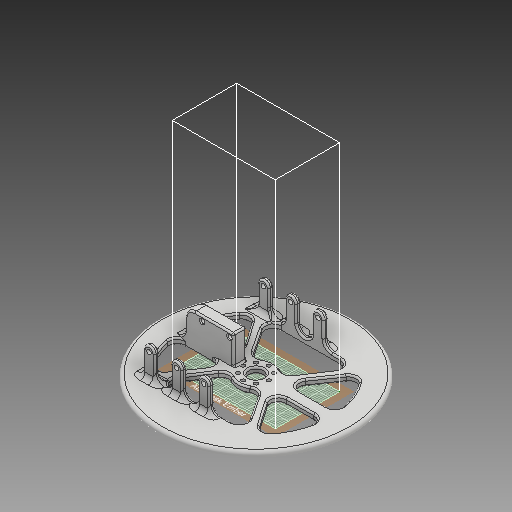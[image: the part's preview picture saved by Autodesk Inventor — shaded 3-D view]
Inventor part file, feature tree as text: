
AUTODESK INVENTOR PART (.ipt)
format: ipt  version: 2018 (Build 220112000, 112)  size: 1,937,920 bytes
history: native  units: mm
features: fillet x7, sketch x4, extrude x4, mirror x2, hole x1, projected_geometry x1
ambient origin geometry x8: Origin, YZ Plane, XZ Plane, XY Plane, X Axis, Y Axis, Z Axis, Center Point
bodies: Solid1 (feature_tree)
feature tree (19):
  sketch  "Sketch1"  dims[d0=120.0mm d1=14.0mm]
  extrude  "Extrusion1"  Depth=14.0mm
  hole  "Hole1"  [1 undecoded]
  extrude  "Extrusion2"  Depth=14.0mm
  mirror  "Mirror1"
  fillet  "Fillet1"  Radius=14.0mm
  fillet  "Fillet2"  Radius=14.0mm
  fillet  "Fillet3"  Radius=14.0mm
  extrude  "Extrusion3"  Depth=1.0mm
  mirror  "Mirror2"
  fillet  "Fillet4"  Radius=8.0mm
  fillet  "Fillet5"  Radius=8.0mm
  extrude  "Extrusion4"  Depth=1.0mm
  fillet  "Fillet6"  Radius=30.0mm
  fillet  "Fillet7"  Radius=34.0mm
  sketch  "Sketch2"  dims[d3=14.0mm d4=8.0mm d5=14.0mm d6=30.0mm]
  projected_geometry  "Projected Loop1"
  sketch  "Sketch3"  dims[d9=30.0mm d10=14.0mm d11=14.0mm d12=14.0mm d13=14.0mm]
  sketch  "Sketch5"  dims[d15=80.0mm d16=9.0mm d17=16.0mm d18=360.0deg d19=22.0mm d20=8.0mm d21=8.0mm d22=30.0mm d23=30.0mm d24=34.0mm d25=4.0mm d26=0.0mm d27=2.4mm d28=6.0mm d29=4.0mm d30=2.0mm d31=90.0deg d32=8.0mm d33=20.594885mm d34=4.0mm d35=0.0mm d36=5.0mm d37=1.0mm d38=2.0mm d41=7.0mm d42=3.0mm d43=0.0mm d44=5.0mm d45=3.0mm d46=1.0mm d47=1.0mm d48=30.0mm d49=18.0mm d50=2.5mm d51=2.5mm d52=0.0mm d53=0.0mm d54=6.0mm d55=1.0mm d56=0.5mm d57=12.5mm d58=7.0mm d60=17.0mm d61=17.0mm d62=15.0mm d63=7.0mm d64=1.0mm]
note: 1 required parameter value undecoded (feature->parameter linkage not recoverable at this tier; creation-order binding heuristic only, values carry confidence <= 0.55)
